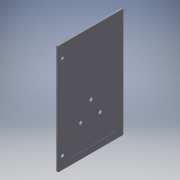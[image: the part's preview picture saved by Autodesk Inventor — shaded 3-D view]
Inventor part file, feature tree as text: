
AUTODESK INVENTOR PART (.ipt)
format: ipt  version: 2017 (Build 210142000, 142)  size: 799,232 bytes
history: native  units: in
note: dims shown in document units (in); Inventor stores cm internally (conversion verified against a paired STEP export)
features: hole x3, other x1
ambient origin geometry x8: Origin, YZ Plane, XZ Plane, XY Plane, X Axis, Y Axis, Z Axis, Center Point
bodies: Solid1 (feature_tree)
feature tree (4):
  other  "nsycrn106250t"
  hole  "Hole1"  [1 undecoded]
  hole  "Hole2"  [1 undecoded]
  hole  "Hole3"  [1 undecoded]
note: 3 required parameter values undecoded (feature->parameter linkage not recoverable at this tier; creation-order binding heuristic only, values carry confidence <= 0.55)
